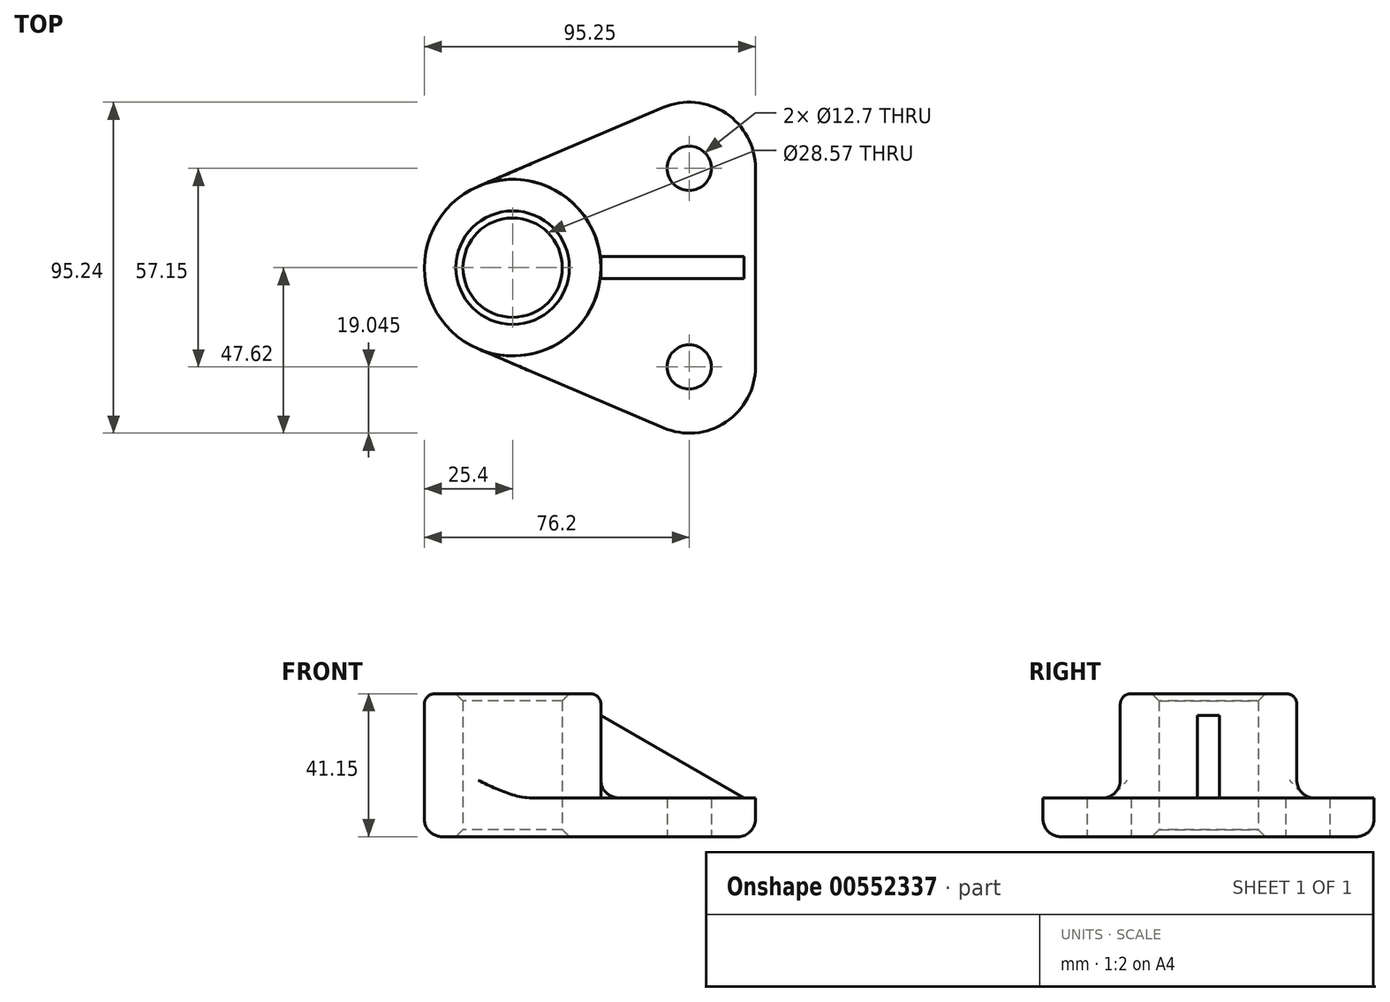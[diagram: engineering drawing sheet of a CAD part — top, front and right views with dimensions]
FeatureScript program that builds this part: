
annotation { "Feature Type Name" : "Feature", "Feature Type Description" : "" }
export const myFeature = defineFeature(function(context is Context, id is Id, definition is map)
    precondition{}
    {
        {
            var Q0;
            Q0=qCreatedBy(makeId("Top.planeOp"),FACE);
            var sketch = newSketch(context, id + "F0", { "sketchPlane" : qUnion([Q0])});
            skCircle(sketch, "E0", {"center": v(0, 0) * mm, "radius": 14.29 * mm});
            skLineSegment(sketch, "E1", {"start": v(-76.8, 0) * mm, "end": v(120.4, 0) * mm, "construction": true});
            skCircle(sketch, "E2", {"center": v(50.8, -28.58) * mm, "radius": 6.35 * mm});
            skArc(sketch, "E3", {"start": v(43.33, -46.1) * mm, "mid": v(61.3, -44.47) * mm, "end": v(69.85, -28.58) * mm});
            skCircle(sketch, "E4", {"center": v(0, 0) * mm, "radius": 25.4 * mm});
            skLineSegment(sketch, "E5", {"start": v(-9.97, -23.36) * mm, "end": v(43.33, -46.1) * mm});
            skCircle(sketch, "E6", {"center": v(50.8, 28.58) * mm, "radius": 6.35 * mm});
            skArc(sketch, "E7", {"start": v(69.85, 28.58) * mm, "mid": v(61.3, 44.47) * mm, "end": v(43.33, 46.1) * mm});
            skLineSegment(sketch, "E8", {"start": v(-9.97, 23.36) * mm, "end": v(43.33, 46.1) * mm});
            skLineSegment(sketch, "E9", {"start": v(69.85, 28.58) * mm, "end": v(69.85, -28.58) * mm});
            skSolve(sketch);
        }
        {
            var Q0;
            Q0=makeQuery(id+"F0.imprint","IMPRINT",FACE,{"disambiguationData":[TD([[makeQuery(id+"F0.imprint","IMPRINT",EDGE,{"derivedFrom":sQuery(id+"F0.wireOp",EDGE,"E0")}),-1.0]])]});
            var Q1;
            Q1=makeQuery(id+"F0.imprint","IMPRINT",FACE,{"disambiguationData":[TD([[makeQuery(id+"F0.imprint","IMPRINT",EDGE,{"derivedFrom":sQuery(id+"F0.wireOp",EDGE,"E2")}),-1.0]])]});
            extrude(context, id + "F1", {"entities" : qUnion([Q0, Q1]), "depth" : 11.18 * mm, "offsetDistance" : 25.4 * mm});
        }
        {
            var Q0;
            Q0=makeQuery(id+"F1.opExtrude","CAP_FACE",FACE,{"disambiguationData":[OSD([sQuery(id+"F0.wireOp",EDGE,"E0"),sQuery(id+"F0.wireOp",EDGE,"E2"),sQuery(id+"F0.wireOp",EDGE,"E3"),sQuery(id+"F0.wireOp",EDGE,"E4"),sQuery(id+"F0.wireOp",EDGE,"E5"),sQuery(id+"F0.wireOp",EDGE,"E6"),sQuery(id+"F0.wireOp",EDGE,"E7"),sQuery(id+"F0.wireOp",EDGE,"E8"),sQuery(id+"F0.wireOp",EDGE,"E9")])],"isStart":false});
            var sketch = newSketch(context, id + "F2", { "sketchPlane" : qUnion([Q0])});
            skCircle(sketch, "E10", {"center": v(0, 0) * mm, "radius": 25.4 * mm});
            skPoint(sketch, "E11", {"position": v(50.8, -28.58) * mm});
            skPoint(sketch, "E12.middle", {"position": v(50.8, 0) * mm});
            skLineSegment(sketch, "E13", {"start": v(69.85, 0) * mm, "end": v(66.55, 0) * mm, "construction": true});
            skLineSegment(sketch, "E14", {"start": v(66.55, 0) * mm, "end": v(25.4, 0) * mm, "construction": true});
            skLineSegment(sketch, "E15.bottom", {"start": v(66.55, -3.17) * mm, "end": v(25.4, -3.17) * mm});
            skLineSegment(sketch, "E15.top", {"start": v(66.55, 3.18) * mm, "end": v(25.4, 3.18) * mm});
            skLineSegment(sketch, "E15.left", {"start": v(66.55, -3.17) * mm, "end": v(66.55, 3.18) * mm});
            skLineSegment(sketch, "E15.right", {"start": v(25.4, -3.17) * mm, "end": v(25.4, 3.18) * mm});
            skPoint(sketch, "E15.middle", {"position": v(45.97, 0) * mm});
            skSolve(sketch);
        }
        {
            var Q0;
            Q0=makeQuery(id+"F2.imprint","IMPRINT",FACE,{"disambiguationData":[TD([[makeQuery(id+"F2.imprint","IMPRINT",EDGE,{"derivedFrom":makeQuery(id+"F1.opExtrude","CAP_EDGE",EDGE,{"disambiguationData":[OSD([sQuery(id+"F0.wireOp",EDGE,"E0")])],"isStart":false})}),-1.0]])]});
            extrude(context, id + "F3", {"entities" : qUnion([Q0]), "operationType" : NewBodyOperationType.ADD, "depth" : 29.97 * mm, "offsetDistance" : 25.4 * mm});
        }
        {
            var Q0;
            Q0=makeQuery(id+"F3.opExtrude","CAP_EDGE",EDGE,{"disambiguationData":[OSD([sQuery(id+"F2.wireOp",EDGE,"E10")])],"isStart":false});
            fillet(context, id + "F4", {"entities" : qUnion([Q0]), "radius" : 3.05 * mm, "tangentPropagation" : true, "allowEdgeOverflow" : false});
        }
        {
            var Q0;
            Q0=makeQuery(id+"F3.opExtrude","CAP_EDGE",EDGE,{"disambiguationData":[OSD([sQuery(id+"F0.wireOp",EDGE,"E0")])],"isStart":false});
            var Q1;
            Q1=makeQuery(id+"F1.opExtrude","CAP_EDGE",EDGE,{"disambiguationData":[OSD([sQuery(id+"F0.wireOp",EDGE,"E0")])],"isStart":true});
            chamfer(context, id + "F5", {"entities" : qUnion([Q0, Q1]), "width" : 2.03 * mm, "tangentPropagation" : true});
        }
        {
            var Q0;
            Q0=makeQuery(id+"F3.boolean.opBoolean","MERGE",FACE,{"derivedFrom":[makeQuery(id+"F1.opExtrude","SWEPT_FACE",FACE,{"disambiguationData":[OSD([sQuery(id+"F0.wireOp",EDGE,"E4")])]}),makeQuery(id+"F3.opExtrude","SWEPT_FACE",FACE,{"disambiguationData":[OSD([sQuery(id+"F2.wireOp",EDGE,"E10")])]})]});
            fillet(context, id + "F6", {"entities" : qUnion([Q0]), "radius" : 5.08 * mm, "tangentPropagation" : true, "allowEdgeOverflow" : false});
        }
        {
            var Q0;
            {var subQ1=sQuery(id+"F2.wireOp",EDGE,"E15.bottom");Q0=makeQuery(id+"F2.imprint","IMPRINT",FACE,{"disambiguationData":[TD([[makeQuery(id+"F2.imprint","IMPRINT",EDGE,{"derivedFrom":subQ1}),-1.0]])]});}
            extrude(context, id + "F7", {"entities" : qUnion([Q0]), "depth" : 30.48 * mm, "offsetDistance" : 25.4 * mm});
        }
        {
            var Q0;
            Q0=makeQuery(id+"F7.opExtrude","SWEPT_FACE",FACE,{"disambiguationData":[OSD([sQuery(id+"F2.wireOp",EDGE,"E15.bottom")])]});
            var sketch = newSketch(context, id + "F8", { "sketchPlane" : qUnion([Q0])});
            skLineSegment(sketch, "E16", {"start": v(66.55, 11.18) * mm, "end": v(25.4, 34.93) * mm});
            skSolve(sketch);
        }
        {
            var Q0;
            Q0=qSketchRegion(id+"F8",true);
            var Q1;
            {var subQ0=sQuery(id+"F8.wireOp",EDGE,"E16");Q1=makeQuery(id+"F8.imprint","IMPRINT",FACE,{"disambiguationData":[TD([[makeQuery(id+"F8.imprint","IMPRINT",EDGE,{"derivedFrom":subQ0}),-1.0]])]});}
            extrude(context, id + "F9", {"entities" : qUnion([Q0, Q1]), "operationType" : NewBodyOperationType.REMOVE, "oppositeDirection" : true, "depth" : 25.4 * mm, "offsetDistance" : 25.4 * mm});
        }
    });
